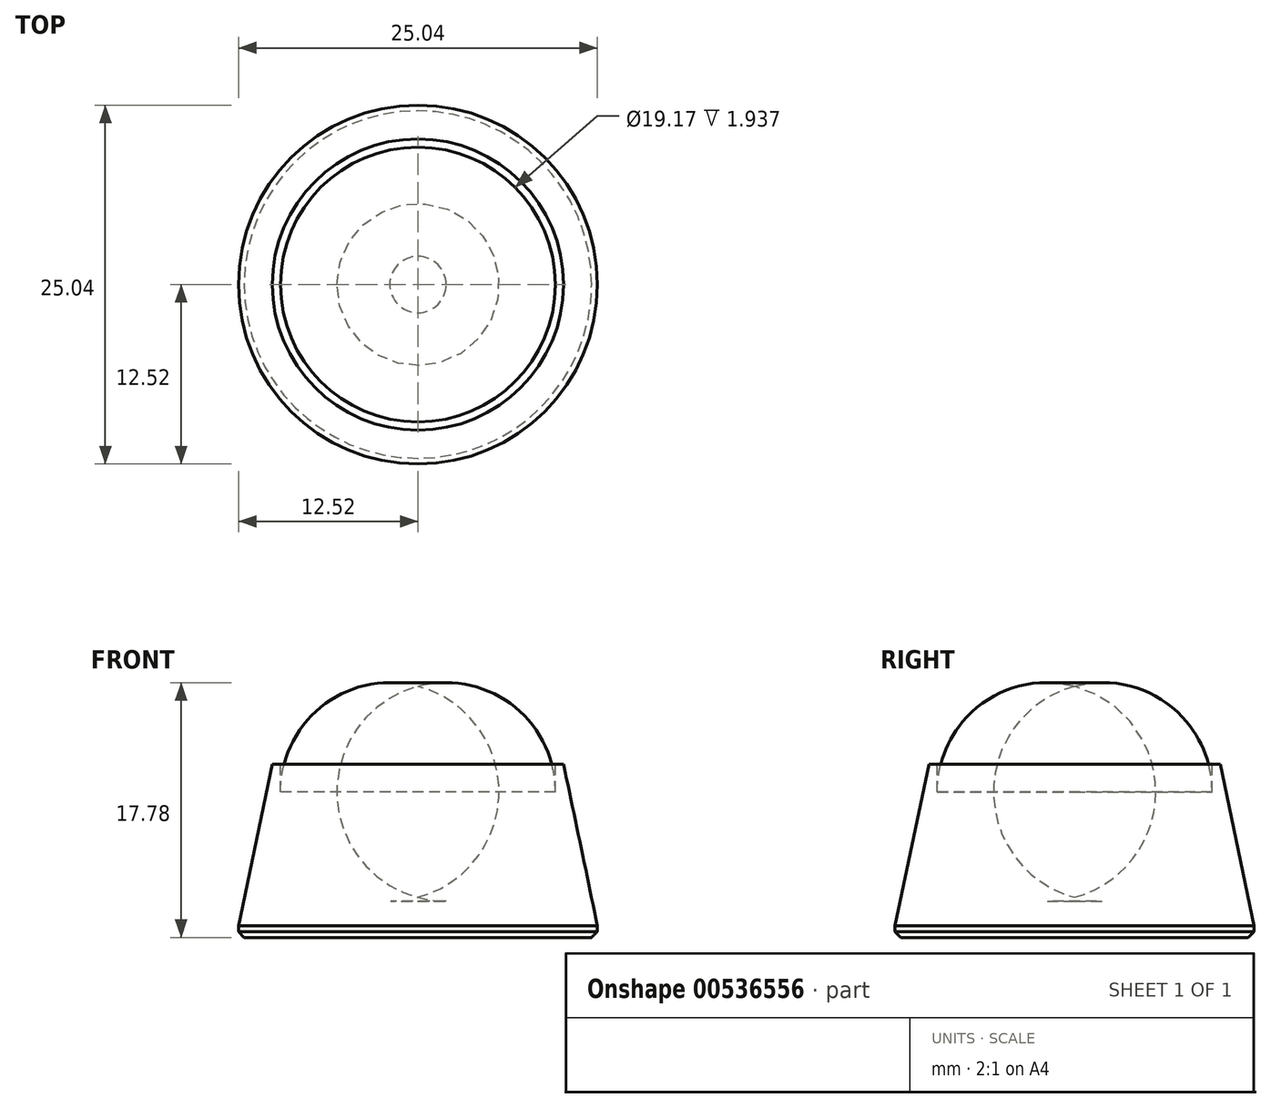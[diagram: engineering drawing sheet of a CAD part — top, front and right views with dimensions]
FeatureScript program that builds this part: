
annotation { "Feature Type Name" : "Feature", "Feature Type Description" : "" }
export const myFeature = defineFeature(function(context is Context, id is Id, definition is map)
    precondition{}
    {
        {
            var Q0;
            Q0=qCreatedBy(makeId("Front.planeOp"),FACE);
            var sketch = newSketch(context, id + "F0", { "sketchPlane" : qUnion([Q0])});
            skLineSegment(sketch, "E0", {"start": v(0, 0) * mm, "end": v(12.12, 0) * mm});
            skLineSegment(sketch, "E1", {"start": v(12.52, 0.4) * mm, "end": v(12.52, 0.81) * mm});
            skLineSegment(sketch, "E2", {"start": v(12.52, 0.81) * mm, "end": v(10.16, 12.1) * mm, "construction": true});
            skLineSegment(sketch, "E3", {"start": v(10.16, 12.1) * mm, "end": v(9.58, 12.1) * mm});
            skLineSegment(sketch, "E4", {"start": v(0, 0) * mm, "end": v(0, 2.54) * mm});
            skLineSegment(sketch, "E5", {"start": v(9.58, 12.1) * mm, "end": v(0, 12.1) * mm, "construction": true});
            skLineSegment(sketch, "E6", {"start": v(0, 12.1) * mm, "end": v(0, 2.54) * mm, "construction": true});
            skLineSegment(sketch, "E7", {"start": v(0, 12.1) * mm, "end": v(10.16, 12.1) * mm, "construction": true});
            skLineSegment(sketch, "E8", {"start": v(10.16, 12.1) * mm, "end": v(12.52, 0.81) * mm});
            skLineSegment(sketch, "E9", {"start": v(12.12, 0) * mm, "end": v(12.52, 0.4) * mm});
            skPoint(sketch, "E10.orphan", {"position": v(12.52, 0) * mm});
            skLineSegment(sketch, "E11", {"start": v(9.58, 12.1) * mm, "end": v(9.58, 10.16) * mm});
            skLineSegment(sketch, "E12", {"start": v(1.96, 2.54) * mm, "end": v(0, 2.54) * mm});
            skPoint(sketch, "E13.visualSharp", {"position": v(9.58, 2.54) * mm});
            skArc(sketch, "E13.filletArc", {"start": v(1.96, 2.54) * mm, "mid": v(7.35, 4.77) * mm, "end": v(9.58, 10.16) * mm});
            skSolve(sketch);
        }
        {
            var Q0;
            Q0=qSketchRegion(id+"F0",true);
            var Q1;
            Q1=sQuery(id+"F0.wireOp",EDGE,"E6");
            revolve(context, id + "F1", {"entities" : qUnion([Q0]), "axis" : qUnion([Q1]), "revolveType" : RevolveType.FULL});
        }
    });
